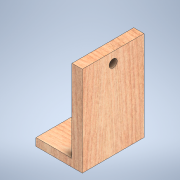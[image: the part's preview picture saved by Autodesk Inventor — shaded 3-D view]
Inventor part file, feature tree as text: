
AUTODESK INVENTOR PART (.ipt)
format: ipt  version: 2021 (Build 250183000, 183)  size: 139,264 bytes
history: native  units: in
note: dims shown in document units (in); Inventor stores cm internally (conversion verified against a paired STEP export)
features: sketch x3, extrude x2, hole x1
ambient origin geometry x8: Origin, YZ Plane, XZ Plane, XY Plane, X Axis, Y Axis, Z Axis, Center Point
bodies: Solid1 (feature_tree)
feature tree (6):
  extrude  "Extrusion1"  Depth=4.5in
  extrude  "Extrusion2"  Depth=1.0in
  hole  "Hole1"  [1 undecoded]
  sketch  "Sketch2"  dims[d1=6.0in d2=4.5in]
  sketch  "Sketch3"  dims[d3=0.75in d4=0.0in d5=1.0in]
  sketch  "Sketch4"  dims[d6=8.0in d7=0.0in d8=1.0in d9=0.781in d10=0.75in d11=1.188in d12=0.75in d13=0.5635in d14=1.0in d15=0.8108in]
note: 1 required parameter value undecoded (feature->parameter linkage not recoverable at this tier; creation-order binding heuristic only, values carry confidence <= 0.55)
